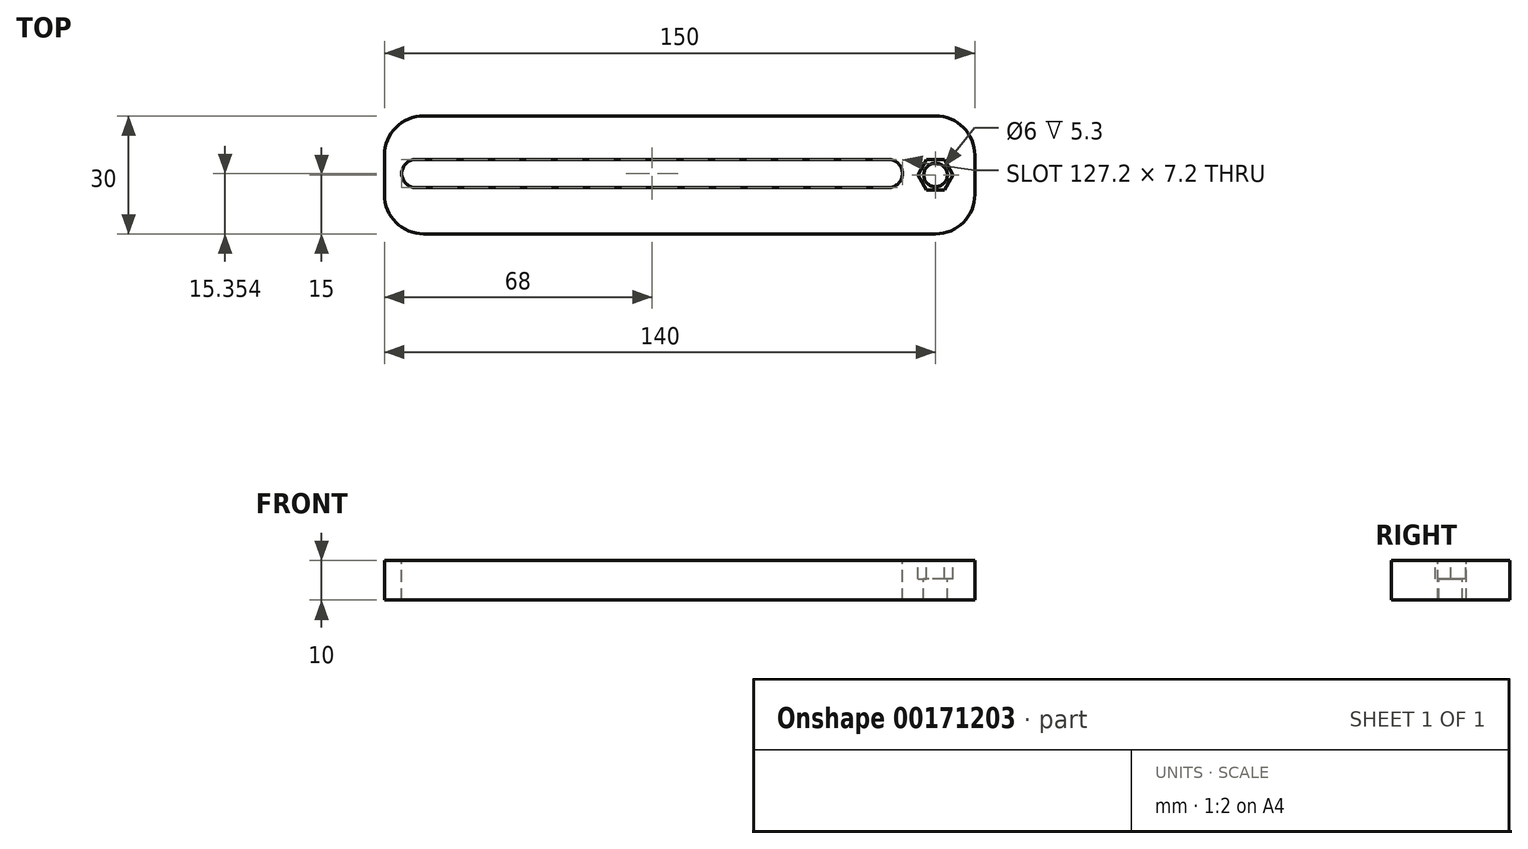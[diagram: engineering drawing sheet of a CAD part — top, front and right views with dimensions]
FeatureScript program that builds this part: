
annotation { "Feature Type Name" : "Feature", "Feature Type Description" : "" }
export const myFeature = defineFeature(function(context is Context, id is Id, definition is map)
    precondition{}
    {
        {
            var Q0;
            Q0=qCreatedBy(makeId("Top.planeOp"),FACE);
            var sketch = newSketch(context, id + "F0", { "sketchPlane" : qUnion([Q0])});
            skLineSegment(sketch, "E0.bottom", {"start": v(-65, -15) * mm, "end": v(65, -15) * mm});
            skLineSegment(sketch, "E0.top", {"start": v(-65, 15) * mm, "end": v(65, 15) * mm});
            skLineSegment(sketch, "E0.left", {"start": v(-75, -5) * mm, "end": v(-75, 5) * mm});
            skLineSegment(sketch, "E0.right", {"start": v(75, -5) * mm, "end": v(75, 5) * mm});
            skPoint(sketch, "E1.visualSharp", {"position": v(-75, 15) * mm});
            skArc(sketch, "E1.filletArc", {"start": v(-65, 15) * mm, "mid": v(-72.07, 12.07) * mm, "end": v(-75, 5) * mm});
            skPoint(sketch, "E2.visualSharp", {"position": v(-75, -15) * mm});
            skArc(sketch, "E2.filletArc", {"start": v(-75, -5) * mm, "mid": v(-72.07, -12.07) * mm, "end": v(-65, -15) * mm});
            skPoint(sketch, "E3.visualSharp", {"position": v(75, -15) * mm});
            skArc(sketch, "E3.filletArc", {"start": v(65, -15) * mm, "mid": v(72.07, -12.07) * mm, "end": v(75, -5) * mm});
            skPoint(sketch, "E4.visualSharp", {"position": v(75, 15) * mm});
            skArc(sketch, "E4.filletArc", {"start": v(75, 5) * mm, "mid": v(72.07, 12.07) * mm, "end": v(65, 15) * mm});
            skSolve(sketch);
        }
        {
            var Q0;
            Q0 = qSketchRegion(id + "F0", true);
            extrude(context, id + "F1", {"entities" : qUnion([Q0]), "depth" : 10 * mm});
        }
        {
            var Q0;
            Q0=makeQuery(id+"F1.opExtrude","CAP_FACE",FACE,{"disambiguationData":[OSD([sQuery(id+"F0.wireOp",EDGE,"E0.bottom"),sQuery(id+"F0.wireOp",EDGE,"E0.top"),sQuery(id+"F0.wireOp",EDGE,"E0.left"),sQuery(id+"F0.wireOp",EDGE,"E0.right"),sQuery(id+"F0.wireOp",EDGE,"E1.filletArc"),sQuery(id+"F0.wireOp",EDGE,"E2.filletArc"),sQuery(id+"F0.wireOp",EDGE,"E3.filletArc"),sQuery(id+"F0.wireOp",EDGE,"E4.filletArc")])],"isStart":false});
            var sketch = newSketch(context, id + "F2", { "sketchPlane" : qUnion([Q0])});
            skCircle(sketch, "E5", {"center": v(65, 0) * mm, "radius": 3 * mm});
            skLineSegment(sketch, "E6.bottom", {"start": v(-67, 3.95) * mm, "end": v(53, 3.95) * mm});
            skLineSegment(sketch, "E6.top", {"start": v(-67, -3.25) * mm, "end": v(53, -3.25) * mm});
            skArc(sketch, "E7", {"start": v(-67, 3.95) * mm, "mid": v(-70.6, 0.35) * mm, "end": v(-67, -3.25) * mm});
            skArc(sketch, "E8", {"start": v(53, -3.25) * mm, "mid": v(56.6, 0.35) * mm, "end": v(53, 3.95) * mm});
            skSolve(sketch);
        }
        {
            var Q0;
            Q0 = qSketchRegion(id + "F2", true);
            extrude(context, id + "F3", {"entities" : qUnion([Q0]), "operationType" : NewBodyOperationType.REMOVE, "endBound" : BoundingType.THROUGH_ALL, "oppositeDirection" : true, "depth" : 25 * mm});
        }
        {
            var Q0;
            Q0=makeQuery(id+"F1.opExtrude","CAP_FACE",FACE,{"disambiguationData":[OSD([sQuery(id+"F0.wireOp",EDGE,"E0.bottom"),sQuery(id+"F0.wireOp",EDGE,"E0.top"),sQuery(id+"F0.wireOp",EDGE,"E0.left"),sQuery(id+"F0.wireOp",EDGE,"E0.right"),sQuery(id+"F0.wireOp",EDGE,"E1.filletArc"),sQuery(id+"F0.wireOp",EDGE,"E2.filletArc"),sQuery(id+"F0.wireOp",EDGE,"E3.filletArc"),sQuery(id+"F0.wireOp",EDGE,"E4.filletArc")])],"isStart":false});
            var sketch = newSketch(context, id + "F4", { "sketchPlane" : qUnion([Q0])});
            skCircle(sketch, "E9.cCircle", {"center": v(65, 0) * mm, "radius": 3.9 * mm, "construction": true});
            skLineSegment(sketch, "E9.0", {"start": v(67.25, -3.9) * mm, "end": v(62.75, -3.9) * mm});
            skLineSegment(sketch, "E9.1", {"start": v(62.75, -3.9) * mm, "end": v(60.5, 0) * mm});
            skLineSegment(sketch, "E9.2", {"start": v(60.5, 0) * mm, "end": v(62.75, 3.9) * mm});
            skLineSegment(sketch, "E9.3", {"start": v(62.75, 3.89) * mm, "end": v(67.25, 3.9) * mm});
            skLineSegment(sketch, "E9.4", {"start": v(67.25, 3.9) * mm, "end": v(69.5, 0) * mm});
            skLineSegment(sketch, "E9.5", {"start": v(69.5, 0) * mm, "end": v(67.25, -3.9) * mm});
            skPoint(sketch, "E9.0.midPoint", {"position": v(65, -3.9) * mm});
            skSolve(sketch);
        }
        {
            var Q0;
            Q0 = qSketchRegion(id + "F4", true);
            extrude(context, id + "F5", {"entities" : qUnion([Q0]), "operationType" : NewBodyOperationType.REMOVE, "oppositeDirection" : true, "depth" : 4.7 * mm});
        }
    });
